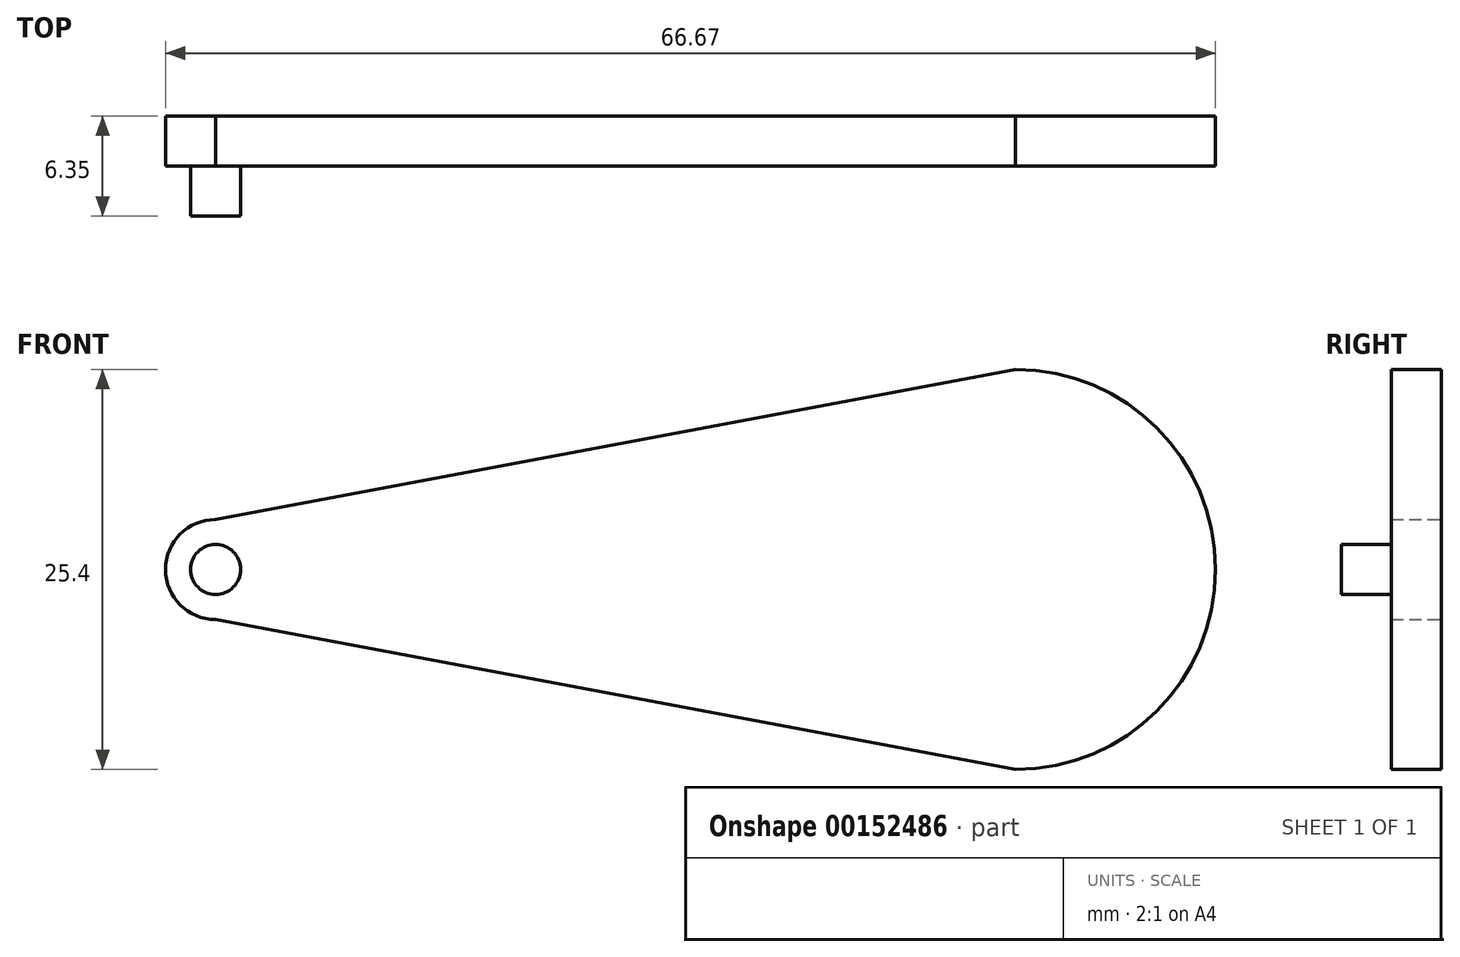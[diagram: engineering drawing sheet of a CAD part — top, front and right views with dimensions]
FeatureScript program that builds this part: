
annotation { "Feature Type Name" : "Feature", "Feature Type Description" : "" }
export const myFeature = defineFeature(function(context is Context, id is Id, definition is map)
    precondition{}
    {
        {
            var Q0;
            Q0=qCreatedBy(makeId("Front.planeOp"),FACE);
            var sketch = newSketch(context, id + "F0", { "sketchPlane" : qUnion([Q0])});
            skArc(sketch, "E0", {"start": v(68.13, -12.7) * mm, "mid": v(80.83, 0) * mm, "end": v(68.13, 12.7) * mm});
            skArc(sketch, "E1", {"start": v(17.33, 3.18) * mm, "mid": v(14.16, 0) * mm, "end": v(17.33, -3.18) * mm});
            skLineSegment(sketch, "E2", {"start": v(17.33, 3.17) * mm, "end": v(68.13, 12.7) * mm});
            skLineSegment(sketch, "E3", {"start": v(17.33, -3.17) * mm, "end": v(68.13, -12.7) * mm});
            skSolve(sketch);
        }
        {
            var Q0;
            Q0=qSketchRegion(id+"F0",true);
            extrude(context, id + "F1", {"entities" : qUnion([Q0]), "depth" : 3.17 * mm});
        }
        {
            var Q0;
            Q0=makeQuery(id+"F1.opExtrude","CAP_FACE",FACE,{"disambiguationData":[OSD([sQuery(id+"F0.wireOp",EDGE,"E0"),sQuery(id+"F0.wireOp",EDGE,"E1"),sQuery(id+"F0.wireOp",EDGE,"E2"),sQuery(id+"F0.wireOp",EDGE,"E3")])],"isStart":false});
            var sketch = newSketch(context, id + "F2", { "sketchPlane" : qUnion([Q0])});
            skCircle(sketch, "E4", {"center": v(17.33, 0) * mm, "radius": 1.59 * mm});
            skSolve(sketch);
        }
        {
            var Q0;
            Q0=qSketchRegion(id+"F2",true);
            extrude(context, id + "F3", {"entities" : qUnion([Q0]), "operationType" : NewBodyOperationType.ADD, "depth" : 3.17 * mm});
        }
    });
